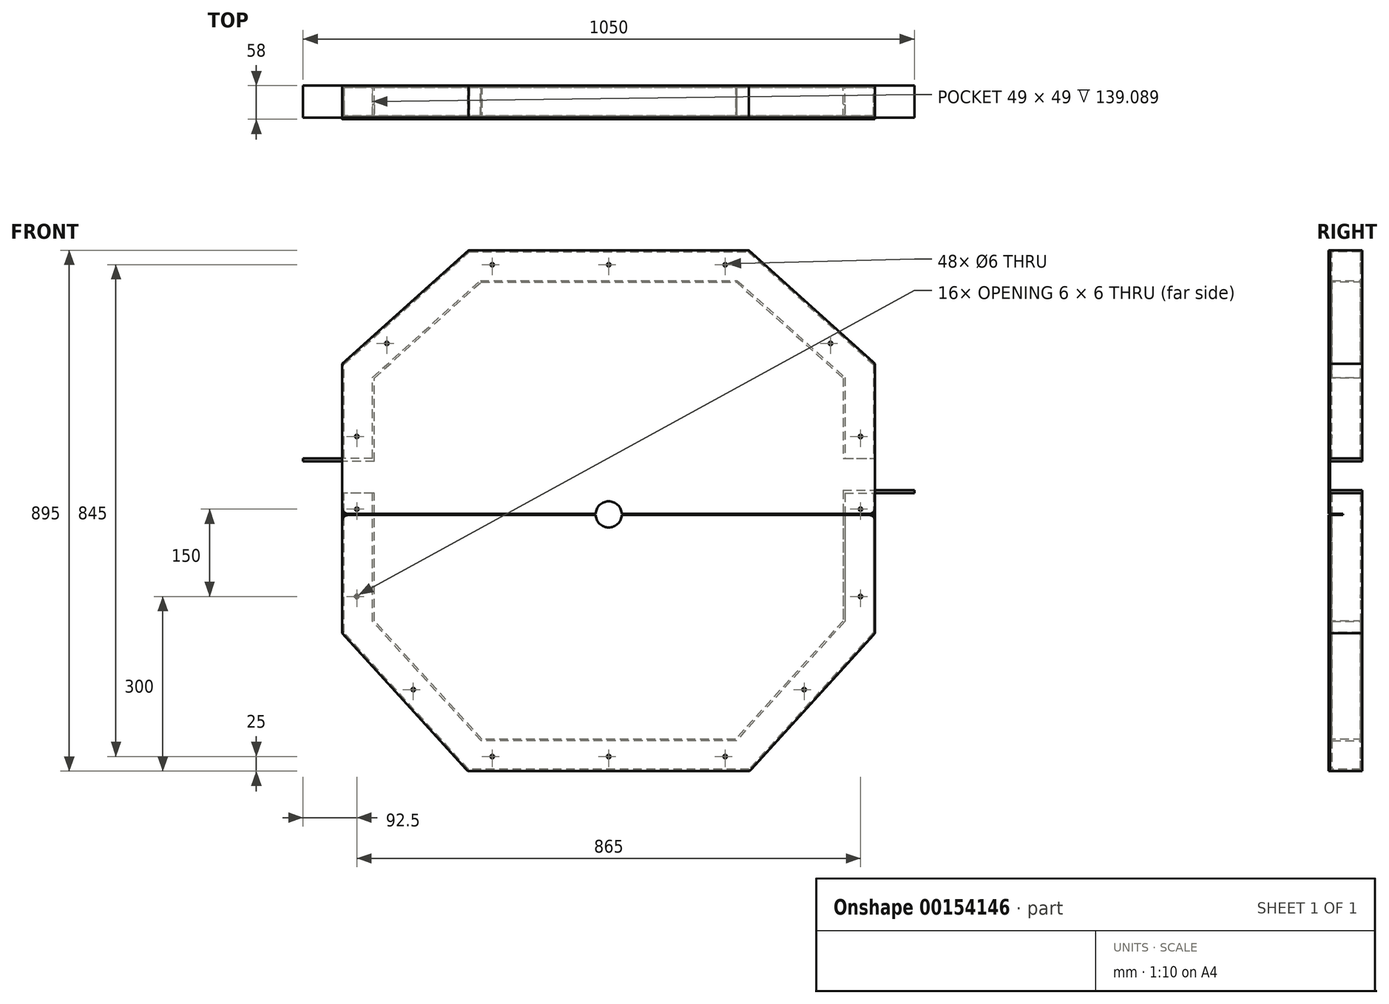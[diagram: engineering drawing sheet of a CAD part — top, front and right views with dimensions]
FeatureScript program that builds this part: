
annotation { "Feature Type Name" : "Feature", "Feature Type Description" : "" }
export const myFeature = defineFeature(function(context is Context, id is Id, definition is map)
    precondition{}
    {
        {
            var Q0;
            Q0=qCreatedBy(makeId("Front.planeOp"),FACE);
            var sketch = newSketch(context, id + "F0", { "sketchPlane" : qUnion([Q0])});
            skLineSegment(sketch, "E0", {"start": v(0, 0) * mm, "end": v(-430, 0) * mm, "construction": true});
            skLineSegment(sketch, "E1", {"start": v(0, 0) * mm, "end": v(430, 0) * mm, "construction": true});
            skPoint(sketch, "E2", {"position": v(0, -330) * mm});
            skLineSegment(sketch, "E3", {"start": v(-430, -330) * mm, "end": v(430, -330) * mm, "construction": true});
            skLineSegment(sketch, "E4", {"start": v(-430, -330) * mm, "end": v(-430, -180) * mm});
            skLineSegment(sketch, "E5", {"start": v(-430, -180) * mm, "end": v(-230, 0) * mm});
            skLineSegment(sketch, "E6", {"start": v(-230, 0) * mm, "end": v(0, 0) * mm});
            skLineSegment(sketch, "E7", {"start": v(0, 0) * mm, "end": v(230, 0) * mm});
            skLineSegment(sketch, "E8", {"start": v(430, -330) * mm, "end": v(430, -180) * mm});
            skLineSegment(sketch, "E9", {"start": v(430, -180) * mm, "end": v(230, 0) * mm});
            skSolve(sketch);
        }
        {
            var Q0;
            Q0=qCreatedBy(makeId("Top.planeOp"),FACE);
            cPlane(context, id + "F1", {"entities" : qUnion([Q0]), "cplaneType" : CPlaneType.OFFSET, "offset" : 330 * mm, "oppositeDirection" : true, "width" : 150 * mm, "height" : 150 * mm});
        }
        {
            var Q0;
            Q0=qCreatedBy(id+"F1.planeOp",FACE);
            var sketch = newSketch(context, id + "F2", { "sketchPlane" : qUnion([Q0])});
            skPoint(sketch, "E10", {"position": v(-430, 0) * mm});
            skLineSegment(sketch, "E11.bottom", {"start": v(-402.5, -27.5) * mm, "end": v(-457.5, -27.5) * mm});
            skLineSegment(sketch, "E11.top", {"start": v(-402.5, 27.5) * mm, "end": v(-457.5, 27.5) * mm});
            skLineSegment(sketch, "E11.left", {"start": v(-402.5, -27.5) * mm, "end": v(-402.5, 27.5) * mm});
            skLineSegment(sketch, "E11.right", {"start": v(-457.5, -27.5) * mm, "end": v(-457.5, 27.5) * mm});
            skLineSegment(sketch, "E12.bottom", {"start": v(-405.5, -24.5) * mm, "end": v(-454.5, -24.5) * mm});
            skLineSegment(sketch, "E12.top", {"start": v(-405.5, 24.5) * mm, "end": v(-454.5, 24.5) * mm});
            skLineSegment(sketch, "E12.left", {"start": v(-405.5, -24.5) * mm, "end": v(-405.5, 24.5) * mm});
            skLineSegment(sketch, "E12.right", {"start": v(-454.5, -24.5) * mm, "end": v(-454.5, 24.5) * mm});
            skSolve(sketch);
        }
        {
            var Q0;
            Q0=makeQuery(id+"F2.imprint","IMPRINT",FACE,{"disambiguationData":[TD([[makeQuery(id+"F2.imprint","IMPRINT",EDGE,{"derivedFrom":sQuery(id+"F2.wireOp",EDGE,"E11.bottom")}),-1.0]])]});
            var Q1;
            Q1=sQuery(id+"F0.wireOp",EDGE,"E4");
            var Q2;
            Q2=sQuery(id+"F0.wireOp",EDGE,"E5");
            var Q3;
            Q3=sQuery(id+"F0.wireOp",EDGE,"E6");
            var Q4;
            Q4=sQuery(id+"F0.wireOp",EDGE,"E7");
            var Q5;
            Q5=sQuery(id+"F0.wireOp",EDGE,"E9");
            var Q6;
            Q6=sQuery(id+"F0.wireOp",EDGE,"E8");
            sweep(context, id + "F3", {"profiles" : qUnion([Q0]), "path" : qUnion([Q1, Q2, Q3, Q4, Q5, Q6])});
        }
        {
            var Q0;
            Q0=makeQuery(id+"F3.opSweep","CAP_FACE",FACE,{"disambiguationData":[OSD([sQuery(id+"F0.wireOp",VERTEX,"E4.start"),sQuery(id+"F2.wireOp",EDGE,"E11.bottom"),sQuery(id+"F2.wireOp",EDGE,"E11.top"),sQuery(id+"F2.wireOp",EDGE,"E11.left"),sQuery(id+"F2.wireOp",EDGE,"E11.right"),sQuery(id+"F2.wireOp",EDGE,"E12.bottom"),sQuery(id+"F2.wireOp",EDGE,"E12.top"),sQuery(id+"F2.wireOp",EDGE,"E12.left"),sQuery(id+"F2.wireOp",EDGE,"E12.right")])],"isStart":true});
            var sketch = newSketch(context, id + "F4", { "sketchPlane" : qUnion([Q0])});
            skLineSegment(sketch, "E13.bottom", {"start": v(-402.5, 27.5) * mm, "end": v(-525, 27.5) * mm});
            skLineSegment(sketch, "E13.top", {"start": v(-402.5, -27.5) * mm, "end": v(-525, -27.5) * mm});
            skLineSegment(sketch, "E13.left", {"start": v(-402.5, 27.5) * mm, "end": v(-402.5, -27.5) * mm});
            skLineSegment(sketch, "E13.right", {"start": v(-525, 27.5) * mm, "end": v(-525, -27.5) * mm});
            skSolve(sketch);
        }
        {
            var Q0;
            Q0 = qSketchRegion(id + "F4", true);
            extrude(context, id + "F5", {"entities" : qUnion([Q0]), "operationType" : NewBodyOperationType.ADD, "depth" : 5 * mm, "offsetDistance" : 25 * mm});
        }
        {
            var Q0;
            Q0=qCreatedBy(id+"F1.planeOp",FACE);
            cPlane(context, id + "F6", {"entities" : qUnion([Q0]), "cplaneType" : CPlaneType.OFFSET, "offset" : 60 * mm, "oppositeDirection" : true, "width" : 150 * mm, "height" : 150 * mm});
        }
        {
            var Q0;
            Q0=qCreatedBy(makeId("Front.planeOp"),FACE);
            var sketch = newSketch(context, id + "F7", { "sketchPlane" : qUnion([Q0])});
            skPoint(sketch, "E14", {"position": v(0, -390) * mm});
            skLineSegment(sketch, "E15", {"start": v(0, -390) * mm, "end": v(-430, -390) * mm, "construction": true});
            skLineSegment(sketch, "E16", {"start": v(0, -390) * mm, "end": v(430, -390) * mm, "construction": true});
            skLineSegment(sketch, "E17", {"start": v(0, -390) * mm, "end": v(0, -840) * mm, "construction": true});
            skLineSegment(sketch, "E18", {"start": v(-430, -390) * mm, "end": v(-430, -620) * mm});
            skLineSegment(sketch, "E19", {"start": v(430, -390) * mm, "end": v(430, -620) * mm});
            skLineSegment(sketch, "E20", {"start": v(0, -840) * mm, "end": v(-230, -840) * mm});
            skLineSegment(sketch, "E21", {"start": v(0, -840) * mm, "end": v(230, -840) * mm});
            skLineSegment(sketch, "E22", {"start": v(230, -840) * mm, "end": v(430, -620) * mm});
            skLineSegment(sketch, "E23", {"start": v(-430, -620) * mm, "end": v(-230, -840) * mm});
            skSolve(sketch);
        }
        {
            var Q0;
            Q0=qCreatedBy(id+"F6.planeOp",FACE);
            var sketch = newSketch(context, id + "F8", { "sketchPlane" : qUnion([Q0])});
            skPoint(sketch, "E24", {"position": v(430, 0) * mm});
            skLineSegment(sketch, "E25.bottom", {"start": v(402.5, -27.5) * mm, "end": v(457.5, -27.5) * mm});
            skLineSegment(sketch, "E25.top", {"start": v(402.5, 27.5) * mm, "end": v(457.5, 27.5) * mm});
            skLineSegment(sketch, "E25.left", {"start": v(402.5, -27.5) * mm, "end": v(402.5, 27.5) * mm});
            skLineSegment(sketch, "E25.right", {"start": v(457.5, -27.5) * mm, "end": v(457.5, 27.5) * mm});
            skLineSegment(sketch, "E26.bottom", {"start": v(405.5, -24.5) * mm, "end": v(454.5, -24.5) * mm});
            skLineSegment(sketch, "E26.top", {"start": v(405.5, 24.5) * mm, "end": v(454.5, 24.5) * mm});
            skLineSegment(sketch, "E26.left", {"start": v(405.5, -24.5) * mm, "end": v(405.5, 24.5) * mm});
            skLineSegment(sketch, "E26.right", {"start": v(454.5, -24.5) * mm, "end": v(454.5, 24.5) * mm});
            skSolve(sketch);
        }
        {
            var Q0;
            Q0=makeQuery(id+"F8.imprint","IMPRINT",FACE,{"disambiguationData":[TD([[makeQuery(id+"F8.imprint","IMPRINT",EDGE,{"derivedFrom":sQuery(id+"F8.wireOp",EDGE,"E25.bottom")}),1.0]])]});
            var Q1;
            Q1=sQuery(id+"F7.wireOp",EDGE,"E19");
            var Q2;
            Q2=sQuery(id+"F7.wireOp",EDGE,"E22");
            var Q3;
            Q3=sQuery(id+"F7.wireOp",EDGE,"E21");
            var Q4;
            Q4=sQuery(id+"F7.wireOp",EDGE,"E20");
            var Q5;
            Q5=sQuery(id+"F7.wireOp",EDGE,"E23");
            var Q6;
            Q6=sQuery(id+"F7.wireOp",EDGE,"E18");
            sweep(context, id + "F9", {"profiles" : qUnion([Q0]), "path" : qUnion([Q1, Q2, Q3, Q4, Q5, Q6])});
        }
        {
            var Q0;
            Q0=makeQuery(id+"F9.opSweep","CAP_FACE",FACE,{"disambiguationData":[OSD([sQuery(id+"F7.wireOp",VERTEX,"E19.start"),sQuery(id+"F8.wireOp",EDGE,"E25.bottom"),sQuery(id+"F8.wireOp",EDGE,"E25.top"),sQuery(id+"F8.wireOp",EDGE,"E25.left"),sQuery(id+"F8.wireOp",EDGE,"E25.right"),sQuery(id+"F8.wireOp",EDGE,"E26.bottom"),sQuery(id+"F8.wireOp",EDGE,"E26.top"),sQuery(id+"F8.wireOp",EDGE,"E26.left"),sQuery(id+"F8.wireOp",EDGE,"E26.right")])],"isStart":true});
            var sketch = newSketch(context, id + "F10", { "sketchPlane" : qUnion([Q0])});
            skLineSegment(sketch, "E27.bottom", {"start": v(402.5, -27.5) * mm, "end": v(525, -27.5) * mm});
            skLineSegment(sketch, "E27.top", {"start": v(402.5, 27.5) * mm, "end": v(525, 27.5) * mm});
            skLineSegment(sketch, "E27.left", {"start": v(402.5, -27.5) * mm, "end": v(402.5, 27.5) * mm});
            skLineSegment(sketch, "E27.right", {"start": v(525, -27.5) * mm, "end": v(525, 27.5) * mm});
            skSolve(sketch);
        }
        {
            var Q0;
            Q0 = qSketchRegion(id + "F10", true);
            extrude(context, id + "F11", {"entities" : qUnion([Q0]), "operationType" : NewBodyOperationType.ADD, "depth" : 5 * mm, "offsetDistance" : 25 * mm});
        }
        {
            var Q0;
            {var subQ0=sQuery(id+"F4.wireOp",EDGE,"E13.bottom");Q0=makeQuery(id+"FolUU5aMUaDlA69_1.1.F5.boolean.opBoolean","MERGE",FACE,{"derivedFrom":[makeQuery(id+"F5.boolean.opBoolean","MERGE",FACE,{"derivedFrom":[makeQuery(id+"F3.opSweep","SWEPT_FACE",FACE,{"disambiguationData":[OSD([sQuery(id+"F0.wireOp",EDGE,"E4"),sQuery(id+"F2.wireOp",EDGE,"E11.bottom")])]}),makeQuery(id+"F5.opExtrude","SWEPT_FACE",FACE,{"disambiguationData":[OSD([subQ0])]})]}),makeQuery(id+"FolUU5aMUaDlA69_1.1.F5.opExtrude","SWEPT_FACE",FACE,{"disambiguationData":[OSD([subQ0])]})]});}
            var sketch = newSketch(context, id + "F12", { "sketchPlane" : qUnion([Q0])});
            skLineSegment(sketch, "E28.0", {"start": v(-457.5, -167.75) * mm, "end": v(-240.55, 27.5) * mm});
            skLineSegment(sketch, "E29.0", {"start": v(-240.55, 27.5) * mm, "end": v(240.55, 27.5) * mm});
            skLineSegment(sketch, "E30.0", {"start": v(240.55, 27.5) * mm, "end": v(457.5, -167.75) * mm});
            skLineSegment(sketch, "E31.0", {"start": v(457.5, -630.63) * mm, "end": v(242.17, -867.5) * mm});
            skLineSegment(sketch, "E32.0", {"start": v(-242.17, -867.5) * mm, "end": v(-457.5, -630.63) * mm});
            skLineSegment(sketch, "E33.0", {"start": v(242.17, -867.5) * mm, "end": v(-242.17, -867.5) * mm});
            skLineSegment(sketch, "E34", {"start": v(-457.5, -167.75) * mm, "end": v(-457.5, -630.63) * mm});
            skLineSegment(sketch, "E35", {"start": v(457.5, -167.75) * mm, "end": v(457.5, -630.63) * mm});
            skSolve(sketch);
        }
        {
            var Q0;
            Q0 = qSketchRegion(id + "F12", true);
            extrude(context, id + "F13", {"entities" : qUnion([Q0]), "depth" : 3 * mm, "offsetDistance" : 25 * mm});
        }
        {
            var Q0;
            Q0=makeQuery(id+"F13.opExtrude","CAP_FACE",FACE,{"disambiguationData":[OSD([sQuery(id+"F12.wireOp",EDGE,"E28.0"),sQuery(id+"F12.wireOp",EDGE,"E29.0"),sQuery(id+"F12.wireOp",EDGE,"E30.0"),sQuery(id+"F12.wireOp",EDGE,"E31.0"),sQuery(id+"F12.wireOp",EDGE,"E32.0"),sQuery(id+"F12.wireOp",EDGE,"E33.0"),sQuery(id+"F12.wireOp",EDGE,"E34"),sQuery(id+"F12.wireOp",EDGE,"E35")])],"isStart":false});
            var sketch = newSketch(context, id + "F14", { "sketchPlane" : qUnion([Q0])});
            skPoint(sketch, "E36", {"position": v(0, -426.5) * mm});
            skPoint(sketch, "E36.positionSnap0", {"position": v(0, -867.5) * mm});
            skCircle(sketch, "E37", {"center": v(0, -426.5) * mm, "radius": 22.5 * mm});
            skLineSegment(sketch, "E38.bottom", {"start": v(475, -425.5) * mm, "end": v(-475, -425.5) * mm});
            skLineSegment(sketch, "E38.top", {"start": v(475, -427.5) * mm, "end": v(-475, -427.5) * mm});
            skLineSegment(sketch, "E38.left", {"start": v(475, -425.5) * mm, "end": v(475, -427.5) * mm});
            skLineSegment(sketch, "E38.right", {"start": v(-475, -425.5) * mm, "end": v(-475, -427.5) * mm});
            skSolve(sketch);
        }
        {
            var Q0;
            Q0 = qSketchRegion(id + "F14", true);
            extrude(context, id + "F15", {"entities" : qUnion([Q0]), "operationType" : NewBodyOperationType.REMOVE, "oppositeDirection" : true, "depth" : 25 * mm, "offsetDistance" : 25 * mm});
        }
        {
            var Q0;
            {var subQ0=sQuery(id+"F12.wireOp",EDGE,"E30.0");var subQ1=sQuery(id+"F12.wireOp",EDGE,"E34");var subQ2=sQuery(id+"F12.wireOp",EDGE,"E29.0");var subQ3=sQuery(id+"F12.wireOp",EDGE,"E28.0");var subQ4=sQuery(id+"F12.wireOp",EDGE,"E35");Q0=makeQuery(id+"F15.boolean.opBoolean","SPLIT",FACE,{"disambiguationData":[TD([makeQuery(id+"F13.opExtrude","SWEPT_FACE",FACE,{"disambiguationData":[OSD([subQ3])]})])],"derivedFrom":makeQuery(id+"F13.opExtrude","CAP_FACE",FACE,{"disambiguationData":[OSD([subQ3,subQ2,subQ0,sQuery(id+"F12.wireOp",EDGE,"E31.0"),sQuery(id+"F12.wireOp",EDGE,"E32.0"),sQuery(id+"F12.wireOp",EDGE,"E33.0"),subQ1,subQ4])],"isStart":false})});}
            var sketch = newSketch(context, id + "F16", { "sketchPlane" : qUnion([Q0])});
            skPoint(sketch, "E39", {"position": v(-200, 2.5) * mm});
            skPoint(sketch, "E40", {"position": v(200, 2.5) * mm});
            skPoint(sketch, "E41", {"position": v(-380.96, -132.5) * mm});
            skPoint(sketch, "E42", {"position": v(380.96, -132.5) * mm});
            skPoint(sketch, "E43", {"position": v(-432.5, -292.5) * mm});
            skPoint(sketch, "E44", {"position": v(432.5, -292.5) * mm});
            skPoint(sketch, "E45", {"position": v(-432.5, -417.5) * mm});
            skPoint(sketch, "E46", {"position": v(432.5, -417.5) * mm});
            skPoint(sketch, "E47", {"position": v(-432.5, -567.5) * mm});
            skPoint(sketch, "E48", {"position": v(432.5, -567.5) * mm});
            skPoint(sketch, "E49", {"position": v(0, 2.5) * mm});
            skPoint(sketch, "E49.positionSnap0", {"position": v(0, 27.5) * mm});
            skPoint(sketch, "E50", {"position": v(0, -842.5) * mm});
            skPoint(sketch, "E51", {"position": v(-200, -842.5) * mm});
            skPoint(sketch, "E52", {"position": v(200, -842.5) * mm});
            skPoint(sketch, "E53", {"position": v(-335.65, -727.5) * mm});
            skPoint(sketch, "E54", {"position": v(335.65, -727.5) * mm});
            skCircle(sketch, "E55", {"center": v(-200, 2.5) * mm, "radius": 3 * mm});
            skCircle(sketch, "E56", {"center": v(0, 2.5) * mm, "radius": 3 * mm});
            skCircle(sketch, "E57", {"center": v(200, 2.5) * mm, "radius": 3 * mm});
            skCircle(sketch, "E58", {"center": v(380.96, -132.5) * mm, "radius": 3 * mm});
            skCircle(sketch, "E59", {"center": v(-380.96, -132.5) * mm, "radius": 3 * mm});
            skCircle(sketch, "E60", {"center": v(-432.5, -292.5) * mm, "radius": 3 * mm});
            skCircle(sketch, "E61", {"center": v(432.5, -292.5) * mm, "radius": 3 * mm});
            skCircle(sketch, "E62", {"center": v(432.5, -417.5) * mm, "radius": 3 * mm});
            skCircle(sketch, "E63", {"center": v(432.5, -567.5) * mm, "radius": 3 * mm});
            skCircle(sketch, "E64", {"center": v(335.65, -727.5) * mm, "radius": 3 * mm});
            skCircle(sketch, "E65", {"center": v(200, -842.5) * mm, "radius": 3 * mm});
            skCircle(sketch, "E66", {"center": v(0, -842.5) * mm, "radius": 3 * mm});
            skCircle(sketch, "E67", {"center": v(-200, -842.5) * mm, "radius": 3 * mm});
            skCircle(sketch, "E68", {"center": v(-335.65, -727.5) * mm, "radius": 3 * mm});
            skCircle(sketch, "E69", {"center": v(-432.5, -567.5) * mm, "radius": 3 * mm});
            skCircle(sketch, "E70", {"center": v(-432.5, -417.5) * mm, "radius": 3 * mm});
            skSolve(sketch);
        }
        {
            var Q0;
            Q0 = qSketchRegion(id + "F16", true);
            extrude(context, id + "F17", {"entities" : qUnion([Q0]), "operationType" : NewBodyOperationType.REMOVE, "oppositeDirection" : true, "depth" : 60 * mm, "offsetDistance" : 25 * mm});
        }
        {
            var Q0;
            Q0=makeQuery(id+"F13.opExtrude","SWEPT_EDGE",EDGE,{"disambiguationData":[OSD([sQuery(id+"F12.wireOp",EDGE,"E30.0"),sQuery(id+"F12.wireOp",EDGE,"E35")])]});
            var Q1;
            {var subQ0=sQuery(id+"F14.wireOp",EDGE,"E38.bottom");var subQ1=sQuery(id+"F12.wireOp",EDGE,"E35");Q1=makeQuery(id+"F15.boolean.opBoolean","INTERSECT",EDGE,{"derivedFrom":[makeQuery(id+"F13.opExtrude","SWEPT_FACE",FACE,{"disambiguationData":[OSD([subQ1])]}),makeQuery(id+"F15.opExtrude","SWEPT_FACE",FACE,{"disambiguationData":[OSD([subQ0]),TDD([makeQuery(id+"F14.imprint","IMPRINT",EDGE,{"disambiguationData":[TD([[makeQuery(id+"F14.imprint","INTERSECT",VERTEX,{"derivedFrom":[subQ0,sQuery(id+"F14.wireOp",EDGE,"E38.left")]}),-1.0]])],"derivedFrom":subQ0}),makeQuery(id+"F14.imprint","IMPRINT",EDGE,{"disambiguationData":[TD([[makeQuery(id+"F14.imprint","INTERSECT",VERTEX,{"disambiguationData":[OD(1.0)],"derivedFrom":[sQuery(id+"F14.wireOp",EDGE,"E37"),subQ0]}),1.0]])],"derivedFrom":subQ0})])]})]});}
            var Q2;
            {var subQ0=sQuery(id+"F14.wireOp",EDGE,"E38.top");var subQ1=sQuery(id+"F12.wireOp",EDGE,"E35");Q2=makeQuery(id+"F15.boolean.opBoolean","INTERSECT",EDGE,{"derivedFrom":[makeQuery(id+"F13.opExtrude","SWEPT_FACE",FACE,{"disambiguationData":[OSD([subQ1])]}),makeQuery(id+"F15.opExtrude","SWEPT_FACE",FACE,{"disambiguationData":[OSD([subQ0]),TDD([makeQuery(id+"F14.imprint","IMPRINT",EDGE,{"disambiguationData":[TD([[makeQuery(id+"F14.imprint","INTERSECT",VERTEX,{"derivedFrom":[subQ0,sQuery(id+"F14.wireOp",EDGE,"E38.left")]}),-1.0]])],"derivedFrom":subQ0}),makeQuery(id+"F14.imprint","IMPRINT",EDGE,{"disambiguationData":[TD([[makeQuery(id+"F14.imprint","INTERSECT",VERTEX,{"disambiguationData":[OD(1.0)],"derivedFrom":[sQuery(id+"F14.wireOp",EDGE,"E37"),subQ0]}),1.0]])],"derivedFrom":subQ0})])]})]});}
            var Q3;
            Q3=makeQuery(id+"F13.opExtrude","SWEPT_EDGE",EDGE,{"disambiguationData":[OSD([sQuery(id+"F12.wireOp",EDGE,"E31.0"),sQuery(id+"F12.wireOp",EDGE,"E35")])]});
            var Q4;
            Q4=makeQuery(id+"F13.opExtrude","SWEPT_EDGE",EDGE,{"disambiguationData":[OSD([sQuery(id+"F12.wireOp",EDGE,"E31.0"),sQuery(id+"F12.wireOp",EDGE,"E33.0")])]});
            var Q5;
            Q5=makeQuery(id+"F13.opExtrude","SWEPT_EDGE",EDGE,{"disambiguationData":[OSD([sQuery(id+"F12.wireOp",EDGE,"E32.0"),sQuery(id+"F12.wireOp",EDGE,"E33.0")])]});
            var Q6;
            Q6=makeQuery(id+"F13.opExtrude","SWEPT_EDGE",EDGE,{"disambiguationData":[OSD([sQuery(id+"F12.wireOp",EDGE,"E32.0"),sQuery(id+"F12.wireOp",EDGE,"E34")])]});
            var Q7;
            {var subQ0=sQuery(id+"F14.wireOp",EDGE,"E38.bottom");var subQ1=sQuery(id+"F12.wireOp",EDGE,"E34");Q7=makeQuery(id+"F15.boolean.opBoolean","INTERSECT",EDGE,{"derivedFrom":[makeQuery(id+"F13.opExtrude","SWEPT_FACE",FACE,{"disambiguationData":[OSD([subQ1])]}),makeQuery(id+"F15.opExtrude","SWEPT_FACE",FACE,{"disambiguationData":[OSD([subQ0]),TDD([makeQuery(id+"F14.imprint","IMPRINT",EDGE,{"disambiguationData":[TD([[makeQuery(id+"F14.imprint","INTERSECT",VERTEX,{"disambiguationData":[OD(0.0)],"derivedFrom":[sQuery(id+"F14.wireOp",EDGE,"E37"),subQ0]}),-1.0]])],"derivedFrom":subQ0}),makeQuery(id+"F14.imprint","IMPRINT",EDGE,{"disambiguationData":[TD([[makeQuery(id+"F14.imprint","INTERSECT",VERTEX,{"derivedFrom":[subQ0,sQuery(id+"F14.wireOp",EDGE,"E38.right")]}),1.0]])],"derivedFrom":subQ0})])]})]});}
            var Q8;
            {var subQ0=sQuery(id+"F14.wireOp",EDGE,"E38.top");var subQ1=sQuery(id+"F12.wireOp",EDGE,"E34");Q8=makeQuery(id+"F15.boolean.opBoolean","INTERSECT",EDGE,{"derivedFrom":[makeQuery(id+"F13.opExtrude","SWEPT_FACE",FACE,{"disambiguationData":[OSD([subQ1])]}),makeQuery(id+"F15.opExtrude","SWEPT_FACE",FACE,{"disambiguationData":[OSD([subQ0]),TDD([makeQuery(id+"F14.imprint","IMPRINT",EDGE,{"disambiguationData":[TD([[makeQuery(id+"F14.imprint","INTERSECT",VERTEX,{"disambiguationData":[OD(0.0)],"derivedFrom":[sQuery(id+"F14.wireOp",EDGE,"E37"),subQ0]}),-1.0]])],"derivedFrom":subQ0}),makeQuery(id+"F14.imprint","IMPRINT",EDGE,{"disambiguationData":[TD([[makeQuery(id+"F14.imprint","INTERSECT",VERTEX,{"derivedFrom":[subQ0,sQuery(id+"F14.wireOp",EDGE,"E38.right")]}),1.0]])],"derivedFrom":subQ0})])]})]});}
            var Q9;
            Q9=makeQuery(id+"F13.opExtrude","SWEPT_EDGE",EDGE,{"disambiguationData":[OSD([sQuery(id+"F12.wireOp",EDGE,"E28.0"),sQuery(id+"F12.wireOp",EDGE,"E34")])]});
            var Q10;
            Q10=makeQuery(id+"F13.opExtrude","SWEPT_EDGE",EDGE,{"disambiguationData":[OSD([sQuery(id+"F12.wireOp",EDGE,"E28.0"),sQuery(id+"F12.wireOp",EDGE,"E29.0")])]});
            var Q11;
            Q11=makeQuery(id+"F13.opExtrude","SWEPT_EDGE",EDGE,{"disambiguationData":[OSD([sQuery(id+"F12.wireOp",EDGE,"E29.0"),sQuery(id+"F12.wireOp",EDGE,"E30.0")])]});
            fillet(context, id + "F18", {"entities" : qUnion([Q0, Q1, Q2, Q3, Q4, Q5, Q6, Q7, Q8, Q9, Q10, Q11]), "radius" : 10 * mm, "tangentPropagation" : true, "allowEdgeOverflow" : false});
        }
    });
